# Revit family: AC-C2T
name_source: partatom
category: Communication Devices
revit_build: Autodesk Revit 2015 (Build: 20160512_0715(x64)
units: mm (PartAtom-declared; Revit-internal decimal feet)

## types (1)
- AC-C2T
    100V Taps = 16, 8, 4, 2
    70V Taps = 16, 8, 4, 2, 1
    Coverage Horizontal = 170.00°
    Coverage Vertical = 170.00°
    Default Elevation = 0 mm
    Depth = 198.5 mm
    Description = 2.75" Full-range, 170° conical Ceiling Mount Loudspeaker
    Enclosure Depth = 177.3 mm
    Enclosure Radius = 71 mm
    Grille Depth = 11.2 mm
    Grille Radius Base = 106.5 mm
    Grille Radius Extent = 101.6 mm
    Impedance = 8
    Manufacturer = QSC
    Manufacturer URL = www.qsc.com
    Middle Depth = 10 mm
    Middle Radius = 90 mm
    Model = AC-C2T
    Power Handling = 16
    Product Documentation Link = https://www.qsc.com
    Product Page URL = https://www.qsc.com
    SPL Max = 102
    Sensitivity = 84
    URL = https://www.qsc.com
    Weight Dimensional (kg) = 6.86
    Weight Dimensional (lb) = 15.1
    Weight Product (kg) = 1.9
    Weight Product (lb) = 4.2
    Width = 213 mm

## geometry (parser evidence)
native form markers: Blend x4, Sweep x2
no freeform markers — native parametric forms only
